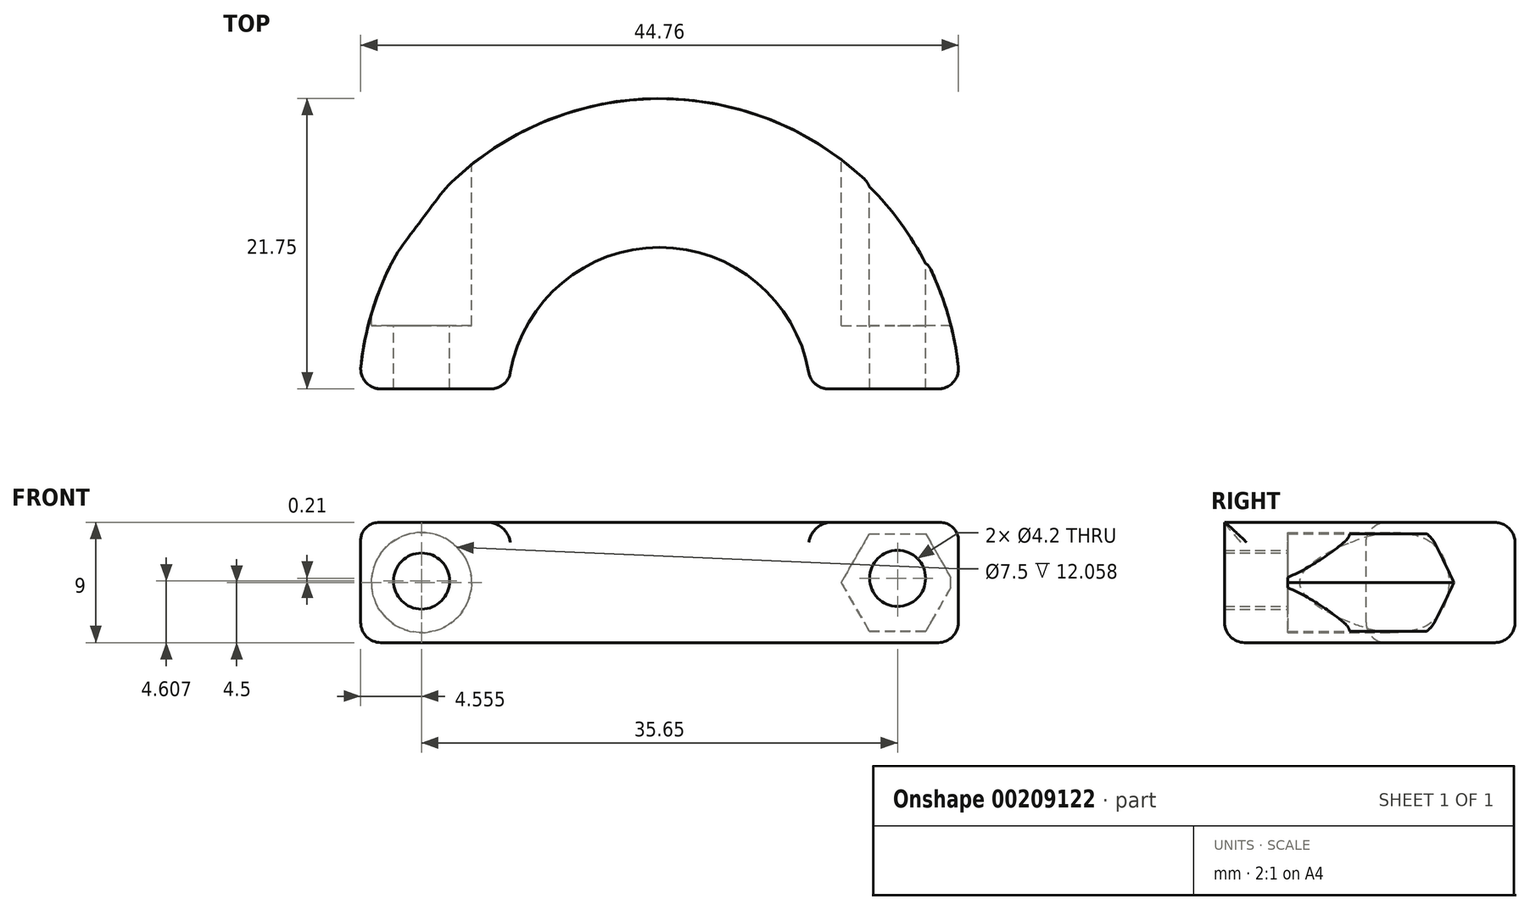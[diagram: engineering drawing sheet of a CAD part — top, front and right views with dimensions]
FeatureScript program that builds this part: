
annotation { "Feature Type Name" : "Feature", "Feature Type Description" : "" }
export const myFeature = defineFeature(function(context is Context, id is Id, definition is map)
    precondition{}
    {
        {
            var Q0;
            Q0=qCreatedBy(makeId("Front.planeOp"),FACE);
            var sketch = newSketch(context, id + "F0", { "sketchPlane" : qUnion([Q0])});
            skLineSegment(sketch, "E0.bottom", {"start": v(-22.5, 0) * mm, "end": v(-11.35, 0) * mm});
            skLineSegment(sketch, "E0.top", {"start": v(-22.5, 9) * mm, "end": v(-11.35, 9) * mm});
            skLineSegment(sketch, "E0.left", {"start": v(-22.5, 0) * mm, "end": v(-22.5, 9) * mm});
            skLineSegment(sketch, "E0.right", {"start": v(-11.35, 0) * mm, "end": v(-11.35, 9) * mm});
            skLineSegment(sketch, "E1", {"start": v(0, 22.22) * mm, "end": v(0, -42.55) * mm});
            skSolve(sketch);
        }
        {
            var Q0;
            Q0=makeQuery(id+"F0.imprint","IMPRINT",FACE,{"disambiguationData":[TD([[makeQuery(id+"F0.imprint","IMPRINT",EDGE,{"derivedFrom":sQuery(id+"F0.wireOp",EDGE,"E0.bottom")}),1.0]])]});
            var Q1;
            Q1=sQuery(id+"F0.wireOp",EDGE,"E1");
            revolve(context, id + "F1", {"entities" : qUnion([Q0]), "axis" : qUnion([Q1]), "revolveType" : RevolveType.FULL});
        }
        {
            var Q0;
            Q0=makeQuery(id+"F1.opRevolve","SWEPT_FACE",FACE,{"disambiguationData":[OSD([sQuery(id+"F0.wireOp",EDGE,"E0.top")])]});
            var sketch = newSketch(context, id + "F2", { "sketchPlane" : qUnion([Q0])});
            skLineSegment(sketch, "E2.bottom", {"start": v(-22.5, 0.75) * mm, "end": v(22.5, 0.75) * mm});
            skLineSegment(sketch, "E2.top", {"start": v(-22.5, -22.5) * mm, "end": v(22.5, -22.5) * mm});
            skLineSegment(sketch, "E2.left", {"start": v(-22.5, 0.75) * mm, "end": v(-22.5, -22.5) * mm});
            skLineSegment(sketch, "E2.right", {"start": v(22.5, 0.75) * mm, "end": v(22.5, -22.5) * mm});
            skSolve(sketch);
        }
        {
            var Q0;
            Q0 = qSketchRegion(id + "F2", true);
            extrude(context, id + "F3", {"entities" : qUnion([Q0]), "operationType" : NewBodyOperationType.REMOVE, "endBound" : BoundingType.THROUGH_ALL, "oppositeDirection" : true, "depth" : 25.4 * mm});
        }
        {
            var Q0;
            Q0=qCreatedBy(makeId("Front.planeOp"),FACE);
            cPlane(context, id + "F4", {"entities" : qUnion([Q0]), "cplaneType" : CPlaneType.OFFSET, "offset" : 22.5 * mm, "oppositeDirection" : true, "width" : 152.4 * mm, "height" : 152.4 * mm});
        }
        {
            var Q0;
            Q0=qCreatedBy(id+"F4.planeOp",FACE);
            var sketch = newSketch(context, id + "F5", { "sketchPlane" : qUnion([Q0])});
            skCircle(sketch, "E3.cCircle", {"center": v(17.83, 4.5) * mm, "radius": 3.65 * mm, "construction": true});
            skLineSegment(sketch, "E3.0", {"start": v(15.72, 8.15) * mm, "end": v(19.93, 8.15) * mm});
            skLineSegment(sketch, "E3.1", {"start": v(19.93, 8.15) * mm, "end": v(22.04, 4.5) * mm});
            skLineSegment(sketch, "E3.2", {"start": v(22.04, 4.5) * mm, "end": v(19.93, 0.85) * mm});
            skLineSegment(sketch, "E3.3", {"start": v(19.93, 0.85) * mm, "end": v(15.72, 0.85) * mm});
            skLineSegment(sketch, "E3.4", {"start": v(15.72, 0.85) * mm, "end": v(13.61, 4.5) * mm});
            skLineSegment(sketch, "E3.5", {"start": v(13.61, 4.5) * mm, "end": v(15.72, 8.15) * mm});
            skPoint(sketch, "E3.0.midPoint", {"position": v(17.83, 8.15) * mm});
            skCircle(sketch, "E4", {"center": v(-17.83, 4.5) * mm, "radius": 3.75 * mm});
            skSolve(sketch);
        }
        {
            var Q0;
            Q0=makeQuery(id+"F5.imprint","IMPRINT",FACE,{"disambiguationData":[TD([[makeQuery(id+"F5.imprint","IMPRINT",EDGE,{"derivedFrom":sQuery(id+"F5.wireOp",EDGE,"E3.0")}),-1.0]])]});
            var Q1;
            Q1=makeQuery(id+"F5.imprint","IMPRINT",FACE,{"disambiguationData":[TD([[makeQuery(id+"F5.imprint","IMPRINT",EDGE,{"derivedFrom":sQuery(id+"F5.wireOp",EDGE,"E4")}),1.0]])]});
            extrude(context, id + "F6", {"entities" : qUnion([Q0, Q1]), "operationType" : NewBodyOperationType.REMOVE, "depth" : 17 * mm});
        }
        {
            var Q0;
            Q0=qCreatedBy(id+"F4.planeOp",FACE);
            var sketch = newSketch(context, id + "F7", { "sketchPlane" : qUnion([Q0])});
            skCircle(sketch, "E5", {"center": v(-17.83, 4.6) * mm, "radius": 2.1 * mm});
            skCircle(sketch, "E6", {"center": v(17.83, 4.82) * mm, "radius": 2.1 * mm});
            skSolve(sketch);
        }
        {
            var Q0;
            Q0=makeQuery(id+"F7.imprint","IMPRINT",FACE,{"disambiguationData":[TD([[makeQuery(id+"F7.imprint","IMPRINT",EDGE,{"derivedFrom":sQuery(id+"F7.wireOp",EDGE,"E6")}),1.0]])]});
            var Q1;
            Q1=makeQuery(id+"F7.imprint","IMPRINT",FACE,{"disambiguationData":[TD([[makeQuery(id+"F7.imprint","IMPRINT",EDGE,{"derivedFrom":sQuery(id+"F7.wireOp",EDGE,"E5")}),1.0]])]});
            extrude(context, id + "F8", {"entities" : qUnion([Q0, Q1]), "operationType" : NewBodyOperationType.REMOVE, "endBound" : BoundingType.THROUGH_ALL, "depth" : 25.4 * mm});
        }
        {
            var Q0;
            Q0=makeQuery(id+"F1.opRevolve","SWEPT_EDGE",EDGE,{"disambiguationData":[OSD([sQuery(id+"F0.wireOp",EDGE,"E0.top"),sQuery(id+"F0.wireOp",EDGE,"E0.left")])]});
            var Q1;
            Q1=makeQuery(id+"F1.opRevolve","SWEPT_EDGE",EDGE,{"disambiguationData":[OSD([sQuery(id+"F0.wireOp",EDGE,"E0.bottom"),sQuery(id+"F0.wireOp",EDGE,"E0.left")])]});
            var Q2;
            Q2=makeQuery(id+"F3.boolean.opBoolean","COPY",EDGE,{"disambiguationData":[OD(1.0)],"derivedFrom":makeQuery(id+"F3.opExtrude","CAP_EDGE",EDGE,{"disambiguationData":[OSD([sQuery(id+"F2.wireOp",EDGE,"E2.bottom")])],"isStart":true})});
            var Q3;
            Q3=makeQuery(id+"F3.boolean.opBoolean","COPY",EDGE,{"disambiguationData":[OD(0.0)],"derivedFrom":makeQuery(id+"F3.opExtrude","CAP_EDGE",EDGE,{"disambiguationData":[OSD([sQuery(id+"F2.wireOp",EDGE,"E2.bottom")])],"isStart":true})});
            var Q4;
            Q4=makeQuery(id+"F1.opRevolve","SWEPT_EDGE",EDGE,{"disambiguationData":[OSD([sQuery(id+"F0.wireOp",EDGE,"E0.top"),sQuery(id+"F0.wireOp",EDGE,"E0.right")])]});
            var Q5;
            Q5=makeQuery(id+"F3.boolean.opBoolean","INTERSECT",EDGE,{"disambiguationData":[OD(0.0)],"derivedFrom":[makeQuery(id+"F1.opRevolve","SWEPT_FACE",FACE,{"disambiguationData":[OSD([sQuery(id+"F0.wireOp",EDGE,"E0.right")])]}),makeQuery(id+"F3.opExtrude","SWEPT_FACE",FACE,{"disambiguationData":[OSD([sQuery(id+"F2.wireOp",EDGE,"E2.bottom")])]})]});
            var Q6;
            Q6=makeQuery(id+"F3.boolean.opBoolean","INTERSECT",EDGE,{"disambiguationData":[OD(1.0)],"derivedFrom":[makeQuery(id+"F1.opRevolve","SWEPT_FACE",FACE,{"disambiguationData":[OSD([sQuery(id+"F0.wireOp",EDGE,"E0.right")])]}),makeQuery(id+"F3.opExtrude","SWEPT_FACE",FACE,{"disambiguationData":[OSD([sQuery(id+"F2.wireOp",EDGE,"E2.bottom")])]})]});
            var Q7;
            Q7=makeQuery(id+"F3.boolean.opBoolean","INTERSECT",EDGE,{"disambiguationData":[OD(0.0)],"derivedFrom":[makeQuery(id+"F1.opRevolve","SWEPT_FACE",FACE,{"disambiguationData":[OSD([sQuery(id+"F0.wireOp",EDGE,"E0.left")])]}),makeQuery(id+"F3.opExtrude","SWEPT_FACE",FACE,{"disambiguationData":[OSD([sQuery(id+"F2.wireOp",EDGE,"E2.bottom")])]})]});
            var Q8;
            Q8=makeQuery(id+"F3.boolean.opBoolean","INTERSECT",EDGE,{"disambiguationData":[OD(1.0)],"derivedFrom":[makeQuery(id+"F1.opRevolve","SWEPT_FACE",FACE,{"disambiguationData":[OSD([sQuery(id+"F0.wireOp",EDGE,"E0.left")])]}),makeQuery(id+"F3.opExtrude","SWEPT_FACE",FACE,{"disambiguationData":[OSD([sQuery(id+"F2.wireOp",EDGE,"E2.bottom")])]})]});
            var Q9;
            Q9=makeQuery(id+"F3.boolean.opBoolean","INTERSECT",EDGE,{"disambiguationData":[OD(1.0)],"derivedFrom":[makeQuery(id+"F1.opRevolve","SWEPT_FACE",FACE,{"disambiguationData":[OSD([sQuery(id+"F0.wireOp",EDGE,"E0.bottom")])]}),makeQuery(id+"F3.opExtrude","SWEPT_FACE",FACE,{"disambiguationData":[OSD([sQuery(id+"F2.wireOp",EDGE,"E2.bottom")])]})]});
            var Q10;
            Q10=makeQuery(id+"F3.boolean.opBoolean","INTERSECT",EDGE,{"disambiguationData":[OD(0.0)],"derivedFrom":[makeQuery(id+"F1.opRevolve","SWEPT_FACE",FACE,{"disambiguationData":[OSD([sQuery(id+"F0.wireOp",EDGE,"E0.bottom")])]}),makeQuery(id+"F3.opExtrude","SWEPT_FACE",FACE,{"disambiguationData":[OSD([sQuery(id+"F2.wireOp",EDGE,"E2.bottom")])]})]});
            var Q11;
            Q11=makeQuery(id+"F1.opRevolve","SWEPT_EDGE",EDGE,{"disambiguationData":[OSD([sQuery(id+"F0.wireOp",EDGE,"E0.bottom"),sQuery(id+"F0.wireOp",EDGE,"E0.right")])]});
            fillet(context, id + "F9", {"entities" : qUnion([Q0, Q1, Q2, Q3, Q4, Q5, Q6, Q7, Q8, Q9, Q10, Q11]), "radius" : 1.5 * mm, "tangentPropagation" : true, "allowEdgeOverflow" : false});
        }
    });
